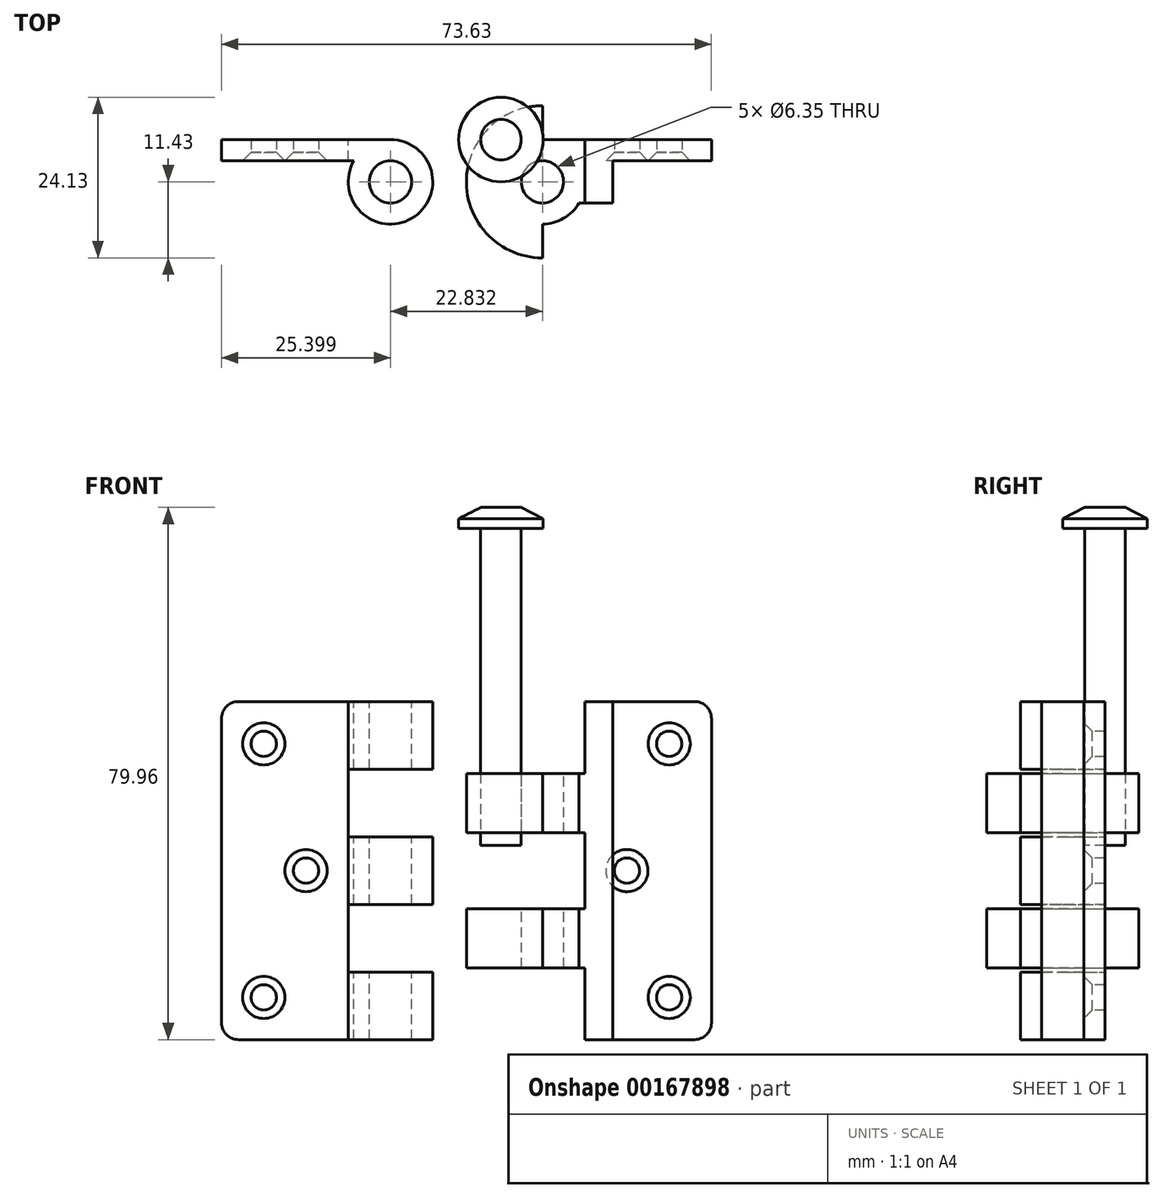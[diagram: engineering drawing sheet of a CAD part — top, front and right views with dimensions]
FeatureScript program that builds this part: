
annotation { "Feature Type Name" : "Feature", "Feature Type Description" : "" }
export const myFeature = defineFeature(function(context is Context, id is Id, definition is map)
    precondition{}
    {
        {
            var Q0;
            Q0=qCreatedBy(makeId("Front.planeOp"),FACE);
            var sketch = newSketch(context, id + "F0", { "sketchPlane" : qUnion([Q0])});
            skLineSegment(sketch, "E0.bottom", {"start": v(-44.61, 38.03) * mm, "end": v(-19.21, 38.03) * mm});
            skLineSegment(sketch, "E0.top", {"start": v(-44.61, -12.77) * mm, "end": v(-19.21, -12.77) * mm});
            skLineSegment(sketch, "E0.left", {"start": v(-44.61, 38.03) * mm, "end": v(-44.61, -12.77) * mm});
            skLineSegment(sketch, "E0.right", {"start": v(-19.21, 38.03) * mm, "end": v(-19.21, -12.77) * mm});
            skSolve(sketch);
        }
        {
            var Q0;
            Q0=qSketchRegion(id+"F0",true);
            extrude(context, id + "F1", {"entities" : qUnion([Q0]), "depth" : 3.17 * mm});
        }
        {
            var Q0;
            Q0=makeQuery(id+"F1.opExtrude","SWEPT_FACE",FACE,{"disambiguationData":[OSD([sQuery(id+"F0.wireOp",EDGE,"E0.bottom")])]});
            var sketch = newSketch(context, id + "F2", { "sketchPlane" : qUnion([Q0])});
            skCircle(sketch, "E1", {"center": v(-19.21, -6.35) * mm, "radius": 6.35 * mm});
            skCircle(sketch, "E2", {"center": v(-19.21, -6.35) * mm, "radius": 3.18 * mm});
            skSolve(sketch);
        }
        {
            var Q0;
            {var subQ5=sQuery(id+"F2.wireOp",EDGE,"E2");Q0=makeQuery(id+"F2.imprint","IMPRINT",FACE,{"disambiguationData":[TD([[makeQuery(id+"F2.imprint","IMPRINT",EDGE,{"derivedFrom":subQ5}),-1.0]])]});}
            var Q1;
            {var subQ1=sQuery(id+"F0.wireOp",EDGE,"E0.bottom");var subQ2=makeQuery(id+"F1.opExtrude","SWEPT_EDGE",EDGE,{"disambiguationData":[OSD([subQ1,sQuery(id+"F0.wireOp",EDGE,"E0.right")])]});Q1=makeQuery(id+"F2.imprint","IMPRINT",FACE,{"disambiguationData":[TD([[makeQuery(id+"F2.imprint","IMPRINT",EDGE,{"derivedFrom":subQ2}),1.0]])]});}
            var Q2;
            Q2=makeQuery(id+"F1.opExtrude","SWEPT_FACE",FACE,{"disambiguationData":[OSD([sQuery(id+"F0.wireOp",EDGE,"E0.top")])]});
            extrude(context, id + "F3", {"entities" : qUnion([Q0, Q1]), "operationType" : NewBodyOperationType.ADD, "endBound" : BoundingType.UP_TO_SURFACE, "oppositeDirection" : true, "endBoundEntityFace" : qUnion([Q2]), "depth" : 25.4 * mm});
        }
        {
            var Q0;
            Q0=makeQuery(id+"F1.opExtrude","CAP_FACE",FACE,{"disambiguationData":[OSD([sQuery(id+"F0.wireOp",EDGE,"E0.bottom"),sQuery(id+"F0.wireOp",EDGE,"E0.top"),sQuery(id+"F0.wireOp",EDGE,"E0.left"),sQuery(id+"F0.wireOp",EDGE,"E0.right")])],"isStart":false});
            var sketch = newSketch(context, id + "F4", { "sketchPlane" : qUnion([Q0])});
            skLineSegment(sketch, "E3", {"start": v(-34.66, 38.03) * mm, "end": v(-34.66, -12.77) * mm, "construction": true});
            skLineSegment(sketch, "E4", {"start": v(-24.7, 12.63) * mm, "end": v(-44.61, 12.63) * mm, "construction": true});
            skLineSegment(sketch, "E5", {"start": v(-24.7, -6.42) * mm, "end": v(-44.61, -6.42) * mm, "construction": true});
            skLineSegment(sketch, "E6", {"start": v(-24.7, 31.68) * mm, "end": v(-44.61, 31.68) * mm, "construction": true});
            skPoint(sketch, "E7", {"position": v(-38.26, 31.68) * mm});
            skPoint(sketch, "E8", {"position": v(-31.91, 12.63) * mm});
            skPoint(sketch, "E9", {"position": v(-38.26, -6.42) * mm});
            skSolve(sketch);
        }
        {
            var Q0;
            Q0=makeQuery(id+"F1.opExtrude","SWEPT_EDGE",EDGE,{"disambiguationData":[OSD([sQuery(id+"F0.wireOp",EDGE,"E0.bottom"),sQuery(id+"F0.wireOp",EDGE,"E0.left")])]});
            var Q1;
            Q1=makeQuery(id+"F1.opExtrude","SWEPT_EDGE",EDGE,{"disambiguationData":[OSD([sQuery(id+"F0.wireOp",EDGE,"E0.top"),sQuery(id+"F0.wireOp",EDGE,"E0.left")])]});
            fillet(context, id + "F5", {"entities" : qUnion([Q0, Q1]), "radius" : 2.54 * mm, "tangentPropagation" : true, "allowEdgeOverflow" : false});
        }
        {
            var Q0;
            Q0=makeQuery(id+"F0.imprint","IMPRINT",FACE,{"disambiguationData":[TD([[makeQuery(id+"F0.imprint","IMPRINT",EDGE,{"derivedFrom":sQuery(id+"F0.wireOp",EDGE,"E0.bottom")}),-1.0]])]});
            var sketch = newSketch(context, id + "F6", { "sketchPlane" : qUnion([Q0])});
            skLineSegment(sketch, "E10", {"start": v(-25.56, -2.61) * mm, "end": v(-12.86, -2.61) * mm});
            skLineSegment(sketch, "E11", {"start": v(-12.86, -2.61) * mm, "end": v(-12.86, 7.55) * mm});
            skLineSegment(sketch, "E12", {"start": v(-12.86, 7.55) * mm, "end": v(-25.56, 7.55) * mm});
            skLineSegment(sketch, "E13", {"start": v(-25.56, 7.55) * mm, "end": v(-25.56, -2.61) * mm});
            skLineSegment(sketch, "E14", {"start": v(-25.56, 17.7) * mm, "end": v(-12.86, 17.7) * mm});
            skLineSegment(sketch, "E15", {"start": v(-12.86, 17.7) * mm, "end": v(-12.86, 27.87) * mm});
            skLineSegment(sketch, "E16", {"start": v(-12.86, 27.87) * mm, "end": v(-25.56, 27.87) * mm});
            skLineSegment(sketch, "E17", {"start": v(-25.56, 27.87) * mm, "end": v(-25.56, 17.7) * mm});
            skPoint(sketch, "E18", {"position": v(-19.21, -2.61) * mm});
            skLineSegment(sketch, "E19", {"start": v(-19.21, 27.87) * mm, "end": v(-19.21, 38.03) * mm});
            skLineSegment(sketch, "E20", {"start": v(-19.21, 17.7) * mm, "end": v(-19.21, 7.55) * mm});
            skLineSegment(sketch, "E21", {"start": v(-19.21, -2.61) * mm, "end": v(-19.21, -12.77) * mm});
            skLineSegment(sketch, "E22", {"start": v(-12.86, 17.7) * mm, "end": v(-12.86, 7.55) * mm});
            skLineSegment(sketch, "E23", {"start": v(-25.56, 7.55) * mm, "end": v(-25.56, 17.7) * mm});
            skLineSegment(sketch, "E24", {"start": v(-25.56, 27.87) * mm, "end": v(-25.56, 38.04) * mm});
            skLineSegment(sketch, "E25", {"start": v(-25.56, 38.04) * mm, "end": v(-12.86, 38.03) * mm});
            skLineSegment(sketch, "E26", {"start": v(-12.86, 38.03) * mm, "end": v(-12.86, 27.87) * mm});
            skLineSegment(sketch, "E27", {"start": v(-12.86, -2.61) * mm, "end": v(-12.86, -12.77) * mm});
            skLineSegment(sketch, "E28", {"start": v(-12.86, -12.77) * mm, "end": v(-25.56, -12.77) * mm});
            skLineSegment(sketch, "E29", {"start": v(-25.56, -12.77) * mm, "end": v(-25.56, -2.61) * mm});
            skSolve(sketch);
        }
        {
            var Q0;
            {var subQ0=sQuery(id+"F6.wireOp",EDGE,"E17");Q0=makeQuery(id+"F6.imprint","IMPRINT",FACE,{"disambiguationData":[TD([[makeQuery(id+"F6.imprint","IMPRINT",EDGE,{"derivedFrom":subQ0}),1.0]])]});}
            var Q1;
            {var subQ0=sQuery(id+"F6.wireOp",EDGE,"E15");Q1=makeQuery(id+"F6.imprint","IMPRINT",FACE,{"disambiguationData":[TD([[makeQuery(id+"F6.imprint","IMPRINT",EDGE,{"derivedFrom":subQ0}),1.0]])]});}
            var Q2;
            {var subQ0=sQuery(id+"F6.wireOp",EDGE,"E13");Q2=makeQuery(id+"F6.imprint","IMPRINT",FACE,{"disambiguationData":[TD([[makeQuery(id+"F6.imprint","IMPRINT",EDGE,{"derivedFrom":subQ0}),1.0]])]});}
            var Q3;
            {var subQ0=sQuery(id+"F6.wireOp",EDGE,"E11");Q3=makeQuery(id+"F6.imprint","IMPRINT",FACE,{"disambiguationData":[TD([[makeQuery(id+"F6.imprint","IMPRINT",EDGE,{"derivedFrom":subQ0}),1.0]])]});}
            extrude(context, id + "F7", {"entities" : qUnion([Q0, Q1, Q2, Q3]), "operationType" : NewBodyOperationType.REMOVE, "depth" : 25.4 * mm});
        }
        {
            var Q0;
            Q0=qCreatedBy(makeId("Front.planeOp"),FACE);
            var sketch = newSketch(context, id + "F8", { "sketchPlane" : qUnion([Q0])});
            skLineSegment(sketch, "E30.bottom", {"start": v(3.62, 38.03) * mm, "end": v(29.02, 38.03) * mm});
            skLineSegment(sketch, "E30.top", {"start": v(3.62, -12.77) * mm, "end": v(29.02, -12.77) * mm});
            skLineSegment(sketch, "E30.left", {"start": v(3.62, 38.03) * mm, "end": v(3.62, -12.77) * mm});
            skLineSegment(sketch, "E30.right", {"start": v(29.02, 38.03) * mm, "end": v(29.02, -12.77) * mm});
            skSolve(sketch);
        }
        {
            var Q0;
            Q0=qSketchRegion(id+"F8",true);
            extrude(context, id + "F9", {"entities" : qUnion([Q0]), "depth" : 3.17 * mm});
        }
        {
            var Q0;
            Q0=makeQuery(id+"F9.opExtrude","SWEPT_FACE",FACE,{"disambiguationData":[OSD([sQuery(id+"F8.wireOp",EDGE,"E30.bottom")])]});
            var sketch = newSketch(context, id + "F10", { "sketchPlane" : qUnion([Q0])});
            skCircle(sketch, "E31", {"center": v(3.62, -6.35) * mm, "radius": 6.35 * mm});
            skCircle(sketch, "E32", {"center": v(3.62, -6.35) * mm, "radius": 3.18 * mm});
            skPoint(sketch, "E33.endSnap0", {"position": v(16.32, -3.18) * mm});
            skLineSegment(sketch, "E34", {"start": v(9.12, -3.18) * mm, "end": v(14.2, -3.18) * mm});
            skLineSegment(sketch, "E35", {"start": v(14.2, -3.18) * mm, "end": v(14.2, -9.53) * mm});
            skLineSegment(sketch, "E36", {"start": v(14.2, -9.53) * mm, "end": v(9.12, -9.53) * mm});
            skArc(sketch, "E37", {"start": v(9.12, -9.53) * mm, "mid": v(9.97, -6.35) * mm, "end": v(9.12, -3.17) * mm});
            skLineSegment(sketch, "E38", {"start": v(3.62, 0) * mm, "end": v(3.62, 5.08) * mm});
            skLineSegment(sketch, "E39", {"start": v(3.62, -12.7) * mm, "end": v(3.62, -17.78) * mm});
            skArc(sketch, "E40", {"start": v(3.62, 5.08) * mm, "mid": v(-7.8, -6.35) * mm, "end": v(3.62, -17.78) * mm});
            skSolve(sketch);
        }
        {
            var Q0;
            {var subQ5=sQuery(id+"F10.wireOp",EDGE,"E32");Q0=makeQuery(id+"F10.imprint","IMPRINT",FACE,{"disambiguationData":[TD([[makeQuery(id+"F10.imprint","IMPRINT",EDGE,{"derivedFrom":subQ5}),-1.0]])]});}
            var Q1;
            {var subQ1=sQuery(id+"F8.wireOp",EDGE,"E30.bottom");var subQ2=makeQuery(id+"F9.opExtrude","SWEPT_EDGE",EDGE,{"disambiguationData":[OSD([subQ1,sQuery(id+"F8.wireOp",EDGE,"E30.left")])]});Q1=makeQuery(id+"F10.imprint","IMPRINT",FACE,{"disambiguationData":[TD([[makeQuery(id+"F10.imprint","IMPRINT",EDGE,{"derivedFrom":subQ2}),-1.0]])]});}
            var Q2;
            {var subQ0=sQuery(id+"F10.wireOp",EDGE,"E34");Q2=makeQuery(id+"F10.imprint","IMPRINT",FACE,{"disambiguationData":[TD([[makeQuery(id+"F10.imprint","IMPRINT",EDGE,{"derivedFrom":subQ0}),-1.0]])]});}
            var Q3;
            {var subQ3=sQuery(id+"F10.wireOp",EDGE,"kVLvFgJq-5OX2-QdSF-DZAH-MA7ZTj6VFglU");Q3=makeQuery(id+"F10.imprint","IMPRINT",FACE,{"disambiguationData":[TD([[makeQuery(id+"F10.imprint","IMPRINT",EDGE,{"derivedFrom":subQ3}),-1.0]])]});}
            var Q4;
            {var subQ0=sQuery(id+"F10.wireOp",EDGE,"E38");Q4=makeQuery(id+"F10.imprint","IMPRINT",FACE,{"disambiguationData":[TD([[makeQuery(id+"F10.imprint","IMPRINT",EDGE,{"derivedFrom":subQ0}),1.0]])]});}
            var Q5;
            Q5=makeQuery(id+"F9.opExtrude","SWEPT_FACE",FACE,{"disambiguationData":[OSD([sQuery(id+"F8.wireOp",EDGE,"E30.top")])]});
            extrude(context, id + "F11", {"entities" : qUnion([Q0, Q1, Q2, Q3, Q4]), "operationType" : NewBodyOperationType.ADD, "endBound" : BoundingType.UP_TO_SURFACE, "oppositeDirection" : true, "endBoundEntityFace" : qUnion([Q5]), "depth" : 25.4 * mm});
        }
        {
            var Q0;
            Q0=makeQuery(id+"F9.opExtrude","CAP_FACE",FACE,{"disambiguationData":[OSD([sQuery(id+"F8.wireOp",EDGE,"E30.bottom"),sQuery(id+"F8.wireOp",EDGE,"E30.top"),sQuery(id+"F8.wireOp",EDGE,"E30.left"),sQuery(id+"F8.wireOp",EDGE,"E30.right")])],"isStart":true});
            var sketch = newSketch(context, id + "F12", { "sketchPlane" : qUnion([Q0])});
            skLineSegment(sketch, "E41", {"start": v(-9.97, 27.23) * mm, "end": v(7.8, 27.23) * mm});
            skLineSegment(sketch, "E42", {"start": v(7.8, 27.23) * mm, "end": v(7.8, 38.03) * mm});
            skLineSegment(sketch, "E43", {"start": v(7.8, 38.03) * mm, "end": v(-9.97, 38.03) * mm});
            skLineSegment(sketch, "E44", {"start": v(-9.97, 27.23) * mm, "end": v(-9.97, 38.03) * mm});
            skLineSegment(sketch, "E45", {"start": v(-9.97, 27.23) * mm, "end": v(-9.97, -12.77) * mm});
            skLineSegment(sketch, "E46", {"start": v(-9.97, -12.77) * mm, "end": v(7.8, -12.77) * mm});
            skLineSegment(sketch, "E47", {"start": v(7.8, -12.77) * mm, "end": v(7.8, 27.23) * mm});
            skLineSegment(sketch, "E48", {"start": v(7.8, 18.34) * mm, "end": v(-9.97, 18.34) * mm});
            skLineSegment(sketch, "E49", {"start": v(-9.97, 6.91) * mm, "end": v(7.8, 6.91) * mm});
            skLineSegment(sketch, "E50", {"start": v(-9.97, -1.98) * mm, "end": v(7.8, -1.98) * mm});
            skSolve(sketch);
        }
        {
            var Q0;
            {var subQ0=sQuery(id+"F12.wireOp",EDGE,"E42");Q0=makeQuery(id+"F12.imprint","IMPRINT",FACE,{"disambiguationData":[TD([[makeQuery(id+"F12.imprint","IMPRINT",EDGE,{"derivedFrom":subQ0}),1.0]])]});}
            var Q1;
            {var subQ0=sQuery(id+"F12.wireOp",EDGE,"E44");Q1=makeQuery(id+"F12.imprint","IMPRINT",FACE,{"disambiguationData":[TD([[makeQuery(id+"F12.imprint","IMPRINT",EDGE,{"derivedFrom":subQ0}),-1.0]])]});}
            var Q2;
            {var subQ0=sQuery(id+"F12.wireOp",EDGE,"E48");var subQ1=sQuery(id+"F12.wireOp",EDGE,"E45");var subQ2=makeQuery(id+"F12.imprint","INTERSECT",VERTEX,{"derivedFrom":[subQ1,subQ0]});Q2=makeQuery(id+"F12.imprint","IMPRINT",FACE,{"disambiguationData":[TD([[makeQuery(id+"F12.imprint","IMPRINT",EDGE,{"disambiguationData":[TD([[subQ2,-1.0]])],"derivedFrom":subQ1}),1.0]])]});}
            var Q3;
            {var subQ0=sQuery(id+"F12.wireOp",EDGE,"E48");var subQ1=sQuery(id+"F12.wireOp",EDGE,"E47");var subQ2=makeQuery(id+"F12.imprint","INTERSECT",VERTEX,{"derivedFrom":[subQ1,subQ0]});Q3=makeQuery(id+"F12.imprint","IMPRINT",FACE,{"disambiguationData":[TD([[makeQuery(id+"F12.imprint","IMPRINT",EDGE,{"disambiguationData":[TD([[subQ2,1.0]])],"derivedFrom":subQ1}),1.0]])]});}
            var Q4;
            {var subQ0=sQuery(id+"F12.wireOp",EDGE,"E46");var subQ3=sQuery(id+"F12.wireOp",EDGE,"E47");var subQ4=makeQuery(id+"F12.imprint","INTERSECT",VERTEX,{"derivedFrom":[subQ0,subQ3]});Q4=makeQuery(id+"F12.imprint","IMPRINT",FACE,{"disambiguationData":[TD([[makeQuery(id+"F12.imprint","IMPRINT",EDGE,{"disambiguationData":[TD([[subQ4,1.0]])],"derivedFrom":subQ0}),1.0]])]});}
            var Q5;
            {var subQ1=sQuery(id+"F12.wireOp",EDGE,"E45");var subQ3=sQuery(id+"F12.wireOp",EDGE,"E50");var subQ4=makeQuery(id+"F12.imprint","INTERSECT",VERTEX,{"derivedFrom":[subQ1,subQ3]});Q5=makeQuery(id+"F12.imprint","IMPRINT",FACE,{"disambiguationData":[TD([[makeQuery(id+"F12.imprint","IMPRINT",EDGE,{"disambiguationData":[TD([[subQ4,-1.0]])],"derivedFrom":subQ3}),-1.0]])]});}
            extrude(context, id + "F13", {"entities" : qUnion([Q0, Q1, Q2, Q3, Q4, Q5]), "operationType" : NewBodyOperationType.REMOVE, "endBound" : BoundingType.SYMMETRIC, "oppositeDirection" : true, "depth" : 50.8 * mm});
        }
        {
            var Q0;
            Q0=qCreatedBy(makeId("Front.planeOp"),FACE);
            var sketch = newSketch(context, id + "F14", { "sketchPlane" : qUnion([Q0])});
            skLineSegment(sketch, "E51", {"start": v(-5.65, 64.02) * mm, "end": v(-5.65, 16.4) * mm});
            skLineSegment(sketch, "E52", {"start": v(-5.65, 16.4) * mm, "end": v(-2.6, 16.4) * mm});
            skLineSegment(sketch, "E53", {"start": v(-2.6, 16.4) * mm, "end": v(-2.6, 67.2) * mm});
            skLineSegment(sketch, "E54", {"start": v(-2.6, 67.2) * mm, "end": v(-5.65, 67.2) * mm});
            skLineSegment(sketch, "E55", {"start": v(-5.65, 67.2) * mm, "end": v(-8.96, 65.52) * mm});
            skLineSegment(sketch, "E56", {"start": v(-8.96, 65.52) * mm, "end": v(-8.96, 64.02) * mm});
            skLineSegment(sketch, "E57", {"start": v(-8.96, 64.02) * mm, "end": v(-5.65, 64.02) * mm});
            skSolve(sketch);
        }
        {
            var Q0;
            Q0=qSketchRegion(id+"F14",true);
            var Q1;
            Q1=sQuery(id+"F14.wireOp",EDGE,"E53");
            revolve(context, id + "F15", {"entities" : qUnion([Q0]), "axis" : qUnion([Q1]), "revolveType" : RevolveType.FULL});
        }
        {
            var Q0;
            Q0=makeQuery(id+"F9.opExtrude","CAP_FACE",FACE,{"disambiguationData":[OSD([sQuery(id+"F8.wireOp",EDGE,"E30.bottom"),sQuery(id+"F8.wireOp",EDGE,"E30.top"),sQuery(id+"F8.wireOp",EDGE,"E30.left"),sQuery(id+"F8.wireOp",EDGE,"E30.right")])],"isStart":false});
            var sketch = newSketch(context, id + "F16", { "sketchPlane" : qUnion([Q0])});
            skLineSegment(sketch, "E58", {"start": v(21.6, 38.03) * mm, "end": v(21.6, -12.77) * mm, "construction": true});
            skLineSegment(sketch, "E59", {"start": v(9.97, 12.63) * mm, "end": v(29.02, 12.63) * mm, "construction": true});
            skPoint(sketch, "E60", {"position": v(16.32, 12.63) * mm});
            skPoint(sketch, "E61", {"position": v(22.67, 31.68) * mm});
            skPoint(sketch, "E62", {"position": v(22.67, -6.42) * mm});
            skSolve(sketch);
        }
        {
            var Q0;
            Q0=sQuery(id+"F4.wireOp",VERTEX,"E7");
            var Q1;
            Q1=sQuery(id+"F4.wireOp",VERTEX,"E8");
            var Q2;
            Q2=sQuery(id+"F4.wireOp",VERTEX,"E9");
            var Q3;
            Q3=makeQuery(id+"F1.opExtrude","SWEPT_BODY",BODY,{"disambiguationData":[OSD([sQuery(id+"F0.wireOp",EDGE,"E0.bottom"),sQuery(id+"F0.wireOp",EDGE,"E0.top"),sQuery(id+"F0.wireOp",EDGE,"E0.left"),sQuery(id+"F0.wireOp",EDGE,"E0.right")])]});
            hole(context, id + "F17", {"style" : HoleStyle.C_SINK, "endStyle" : HoleEndStyle.THROUGH, "holeDiameter" : 3.8 * mm, "cSinkDiameter" : 6.35 * mm, "cSinkAngle" : 90 * degree, "locations" : qUnion([Q0, Q1, Q2]), "scope" : qUnion([Q3]), "isTappedThrough" : true});
        }
        {
            var Q0;
            Q0=sQuery(id+"F16.wireOp",VERTEX,"E61");
            var Q1;
            Q1=sQuery(id+"F16.wireOp",VERTEX,"E60");
            var Q2;
            Q2=sQuery(id+"F16.wireOp",VERTEX,"E62");
            var Q3;
            Q3=makeQuery(id+"F9.opExtrude","SWEPT_BODY",BODY,{"disambiguationData":[OSD([sQuery(id+"F8.wireOp",EDGE,"E30.bottom"),sQuery(id+"F8.wireOp",EDGE,"E30.top"),sQuery(id+"F8.wireOp",EDGE,"E30.left"),sQuery(id+"F8.wireOp",EDGE,"E30.right")])]});
            hole(context, id + "F18", {"style" : HoleStyle.C_SINK, "endStyle" : HoleEndStyle.THROUGH, "holeDiameter" : 3.8 * mm, "cSinkDiameter" : 6.35 * mm, "cSinkAngle" : 90 * degree, "locations" : qUnion([Q0, Q1, Q2]), "scope" : qUnion([Q3]), "isTappedThrough" : true});
        }
        {
            var Q0;
            Q0=makeQuery(id+"F9.opExtrude","SWEPT_EDGE",EDGE,{"disambiguationData":[OSD([sQuery(id+"F8.wireOp",EDGE,"E30.bottom"),sQuery(id+"F8.wireOp",EDGE,"E30.right")])]});
            var Q1;
            Q1=makeQuery(id+"F9.opExtrude","SWEPT_EDGE",EDGE,{"disambiguationData":[OSD([sQuery(id+"F8.wireOp",EDGE,"E30.top"),sQuery(id+"F8.wireOp",EDGE,"E30.right")])]});
            fillet(context, id + "F19", {"entities" : qUnion([Q0, Q1]), "radius" : 2.54 * mm, "tangentPropagation" : true, "allowEdgeOverflow" : false});
        }
    });
